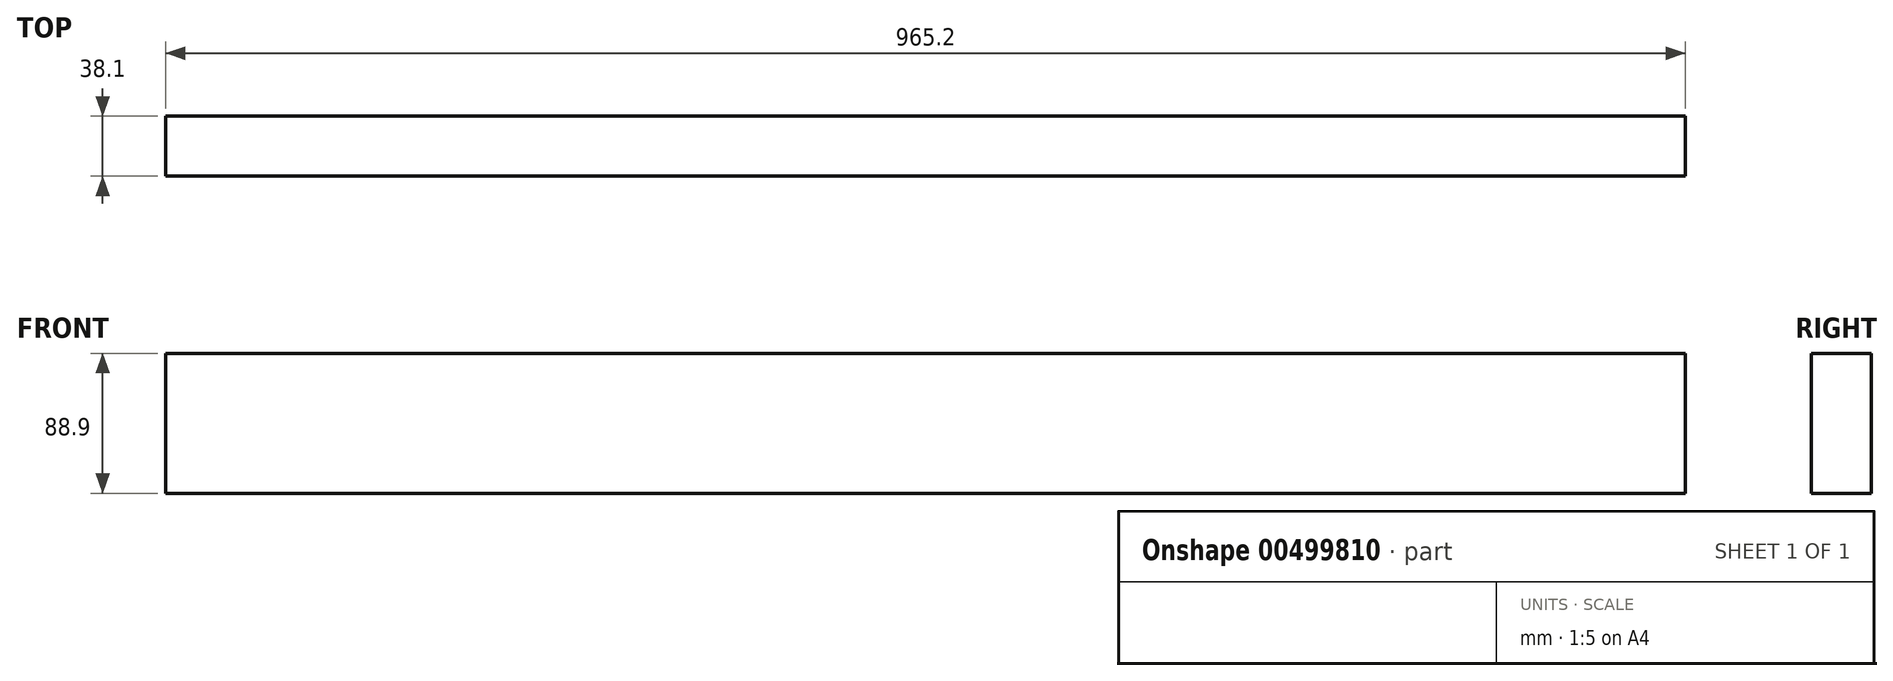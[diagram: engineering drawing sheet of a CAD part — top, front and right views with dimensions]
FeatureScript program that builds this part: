
annotation { "Feature Type Name" : "Feature", "Feature Type Description" : "" }
export const myFeature = defineFeature(function(context is Context, id is Id, definition is map)
    precondition{}
    {
        {
            var Q0;
            Q0=qCreatedBy(makeId("Front.planeOp"),FACE);
            var sketch = newSketch(context, id + "F0", { "sketchPlane" : qUnion([Q0])});
            skLineSegment(sketch, "E0.bottom", {"start": v(482.6, -44.45) * mm, "end": v(-482.6, -44.45) * mm});
            skLineSegment(sketch, "E0.top", {"start": v(482.6, 44.45) * mm, "end": v(-482.6, 44.45) * mm});
            skLineSegment(sketch, "E0.left", {"start": v(482.6, -44.45) * mm, "end": v(482.6, 44.45) * mm});
            skLineSegment(sketch, "E0.right", {"start": v(-482.6, -44.45) * mm, "end": v(-482.6, 44.45) * mm});
            skPoint(sketch, "E0.middle", {"position": v(0, 0) * mm});
            skSolve(sketch);
        }
        {
            var Q0;
            Q0 = qSketchRegion(id + "F0", true);
            extrude(context, id + "F1", {"entities" : qUnion([Q0]), "depth" : 38.1 * mm});
        }
    });
